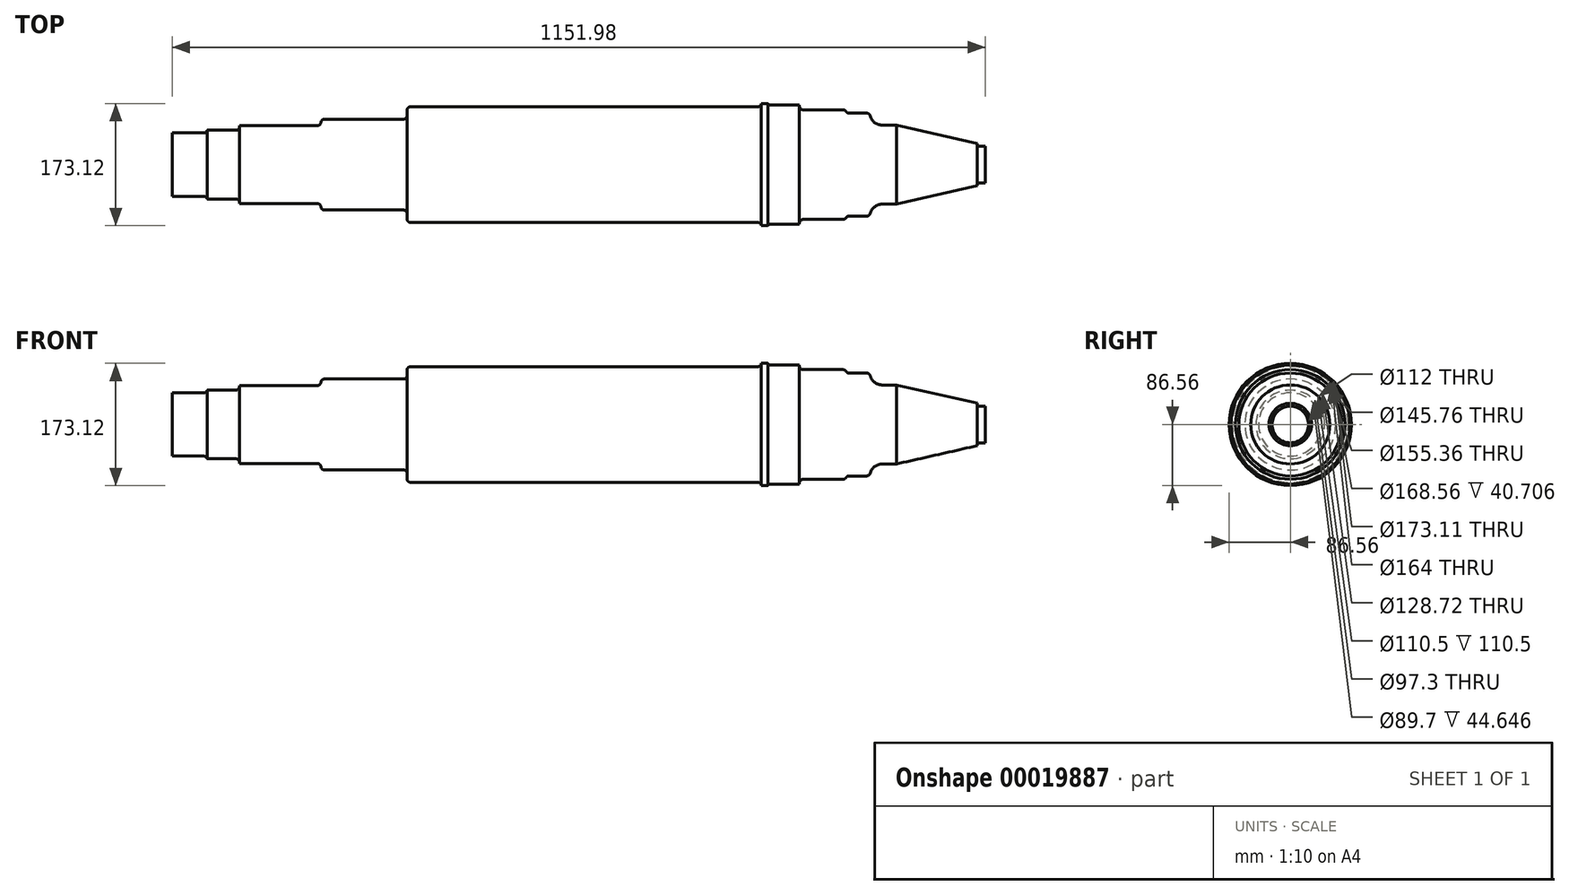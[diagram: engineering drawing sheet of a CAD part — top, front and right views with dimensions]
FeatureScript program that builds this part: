
annotation { "Feature Type Name" : "Feature", "Feature Type Description" : "" }
export const myFeature = defineFeature(function(context is Context, id is Id, definition is map)
    precondition{}
    {
        {
            var Q0;
            Q0=qCreatedBy(makeId("Front.planeOp"),FACE);
            var sketch = newSketch(context, id + "F0", { "sketchPlane" : qUnion([Q0])});
            skLineSegment(sketch, "E0", {"start": v(-457.72, 0) * mm, "end": v(-457.72, 44.85) * mm});
            skLineSegment(sketch, "E1", {"start": v(-457.72, 44.85) * mm, "end": v(-408.22, 44.85) * mm});
            skLineSegment(sketch, "E2", {"start": v(-408.22, 44.85) * mm, "end": v(-408.22, 48.65) * mm});
            skLineSegment(sketch, "E3", {"start": v(-408.22, 48.65) * mm, "end": v(-362.52, 48.65) * mm});
            skLineSegment(sketch, "E4", {"start": v(-362.52, 48.65) * mm, "end": v(-362.52, 55.25) * mm});
            skLineSegment(sketch, "E5", {"start": v(-362.52, 55.25) * mm, "end": v(-247.02, 55.25) * mm});
            skLineSegment(sketch, "E6", {"start": v(-247.02, 55.25) * mm, "end": v(-247.02, 64.36) * mm});
            skLineSegment(sketch, "E7", {"start": v(-247.02, 64.36) * mm, "end": v(-125.02, 64.36) * mm});
            skLineSegment(sketch, "E8", {"start": v(-125.02, 64.36) * mm, "end": v(-125.02, 82) * mm});
            skLineSegment(sketch, "E9", {"start": v(-125.02, 82) * mm, "end": v(376.98, 82) * mm});
            skLineSegment(sketch, "E10", {"start": v(376.98, 82) * mm, "end": v(376.98, 86.56) * mm});
            skLineSegment(sketch, "E11", {"start": v(376.98, 86.56) * mm, "end": v(386.1, 86.56) * mm});
            skLineSegment(sketch, "E12", {"start": v(386.1, 86.56) * mm, "end": v(386.1, 84.28) * mm});
            skLineSegment(sketch, "E13", {"start": v(386.1, 84.28) * mm, "end": v(431, 84.28) * mm});
            skLineSegment(sketch, "E14", {"start": v(431, 84.28) * mm, "end": v(431, 77.68) * mm});
            skLineSegment(sketch, "E15", {"start": v(431, 77.68) * mm, "end": v(496.26, 77.68) * mm});
            skLineSegment(sketch, "E16", {"start": v(496.26, 77.68) * mm, "end": v(496.26, 72.88) * mm});
            skLineSegment(sketch, "E17", {"start": v(496.26, 72.88) * mm, "end": v(531.26, 72.88) * mm});
            skLineSegment(sketch, "E18", {"start": v(531.26, 72.88) * mm, "end": v(531.26, 56) * mm});
            skLineSegment(sketch, "E19", {"start": v(-457.72, 0) * mm, "end": v(396.58, 0) * mm});
            skLineSegment(sketch, "E20", {"start": v(682.77, 25.86) * mm, "end": v(694.26, 26.1) * mm});
            skLineSegment(sketch, "E21", {"start": v(682.68, 30.06) * mm, "end": v(682.77, 25.86) * mm});
            skLineSegment(sketch, "E22", {"start": v(562, 0) * mm, "end": v(396.58, 0) * mm});
            skLineSegment(sketch, "E23", {"start": v(-502.65, 0) * mm, "end": v(562, 0) * mm, "construction": true});
            skPoint(sketch, "E23.startSnap0", {"position": v(-30.57, 0) * mm});
            skPoint(sketch, "E23.endSnap0", {"position": v(-30.57, 0) * mm});
            skLineSegment(sketch, "E24", {"start": v(732.2, 0) * mm, "end": v(-530.75, 0) * mm, "construction": true});
            skLineSegment(sketch, "E25", {"start": v(568.26, 56) * mm, "end": v(531.26, 56) * mm});
            skLineSegment(sketch, "E26", {"start": v(568.26, 56) * mm, "end": v(682.68, 30.06) * mm});
            skLineSegment(sketch, "E27", {"start": v(562, 0) * mm, "end": v(683.65, 0) * mm});
            skLineSegment(sketch, "E28", {"start": v(568.26, 56) * mm, "end": v(568.26, -19.91) * mm, "construction": true});
            skLineSegment(sketch, "E29", {"start": v(694.26, 26.1) * mm, "end": v(694.26, 0) * mm});
            skSolve(sketch);
        }
        {
            var Q0;
            Q0=sQuery(id+"F0.wireOp",EDGE,"E0");
            var Q1;
            Q1=sQuery(id+"F0.wireOp",EDGE,"E1");
            var Q2;
            Q2=sQuery(id+"F0.wireOp",EDGE,"E3");
            var Q3;
            Q3=sQuery(id+"F0.wireOp",EDGE,"E2");
            var Q4;
            Q4=sQuery(id+"F0.wireOp",EDGE,"E4");
            var Q5;
            Q5=sQuery(id+"F0.wireOp",EDGE,"E5");
            var Q6;
            Q6=sQuery(id+"F0.wireOp",EDGE,"E6");
            var Q7;
            Q7=sQuery(id+"F0.wireOp",EDGE,"E7");
            var Q8;
            Q8=sQuery(id+"F0.wireOp",EDGE,"E8");
            var Q9;
            Q9=sQuery(id+"F0.wireOp",EDGE,"E9");
            var Q10;
            Q10=sQuery(id+"F0.wireOp",EDGE,"E11");
            var Q11;
            Q11=sQuery(id+"F0.wireOp",EDGE,"E10");
            var Q12;
            Q12=sQuery(id+"F0.wireOp",EDGE,"E12");
            var Q13;
            Q13=sQuery(id+"F0.wireOp",EDGE,"E13");
            var Q14;
            Q14=sQuery(id+"F0.wireOp",EDGE,"E14");
            var Q15;
            Q15=sQuery(id+"F0.wireOp",EDGE,"E15");
            var Q16;
            Q16=sQuery(id+"F0.wireOp",EDGE,"E16");
            var Q17;
            Q17=sQuery(id+"F0.wireOp",EDGE,"E17");
            var Q18;
            Q18=sQuery(id+"F0.wireOp",EDGE,"E18");
            var Q19;
            Q19=sQuery(id+"F0.wireOp",EDGE,"1ff863c3-3cfa-4d4c-a43b-59d3ef948760");
            var Q20;
            Q20=sQuery(id+"F0.wireOp",EDGE,"E20");
            var Q21;
            Q21=sQuery(id+"F0.wireOp",EDGE,"E21");
            var Q22;
            Q22=sQuery(id+"F0.wireOp",EDGE,"605e6a14-245b-47b4-8274-c8cc4451a2e7");
            var Q23;
            Q23=sQuery(id+"F0.wireOp",EDGE,"E26");
            var Q24;
            Q24=sQuery(id+"F0.wireOp",EDGE,"E25");
            var Q25;
            Q25=sQuery(id+"F0.wireOp",EDGE,"E19");
            revolve(context, id + "F1", {"bodyType" : ToolBodyType.SURFACE, "surfaceEntities" : qUnion([Q0, Q1, Q2, Q3, Q4, Q5, Q6, Q7, Q8, Q9, Q10, Q11, Q12, Q13, Q14, Q15, Q16, Q17, Q18, Q19, Q20, Q21, Q22, Q23, Q24]), "axis" : qUnion([Q25]), "revolveType" : RevolveType.FULL});
        }
        {
            var Q0;
            Q0=makeQuery(id+"F1.opRevolve","SWEPT_EDGE",EDGE,{"disambiguationData":[OSD([sQuery(id+"F0.wireOp",VERTEX,"E2.start")])]});
            var Q1;
            Q1=makeQuery(id+"F1.opRevolve","SWEPT_EDGE",EDGE,{"disambiguationData":[OSD([sQuery(id+"F0.wireOp",VERTEX,"E4.start")])]});
            var Q2;
            Q2=makeQuery(id+"F1.opRevolve","SWEPT_EDGE",EDGE,{"disambiguationData":[OSD([sQuery(id+"F0.wireOp",VERTEX,"E6.start")])]});
            var Q3;
            Q3=makeQuery(id+"F1.opRevolve","SWEPT_EDGE",EDGE,{"disambiguationData":[OSD([sQuery(id+"F0.wireOp",VERTEX,"E8.start")])]});
            var Q4;
            Q4=makeQuery(id+"F1.opRevolve","SWEPT_EDGE",EDGE,{"disambiguationData":[OSD([sQuery(id+"F0.wireOp",VERTEX,"E10.start")])]});
            var Q5;
            Q5=makeQuery(id+"F1.opRevolve","SWEPT_FACE",FACE,{"disambiguationData":[OSD([sQuery(id+"F0.wireOp",EDGE,"E17")])]});
            var Q6;
            Q6=makeQuery(id+"F1.opRevolve","SWEPT_EDGE",EDGE,{"disambiguationData":[OSD([sQuery(id+"F0.wireOp",VERTEX,"E15.start")])]});
            var Q7;
            Q7=makeQuery(id+"F1.opRevolve","SWEPT_EDGE",EDGE,{"disambiguationData":[OSD([sQuery(id+"F0.wireOp",VERTEX,"E13.start")])]});
            fillet(context, id + "F2", {"entities" : qUnion([Q0, Q1, Q2, Q3, Q4, Q5, Q6, Q7]), "radius" : 5 * mm, "tangentPropagation" : true, "allowEdgeOverflow" : false});
        }
        {
            var Q0;
            Q0=makeQuery(id+"F1.opRevolve","SWEPT_EDGE",EDGE,{"disambiguationData":[OSD([sQuery(id+"F0.wireOp",VERTEX,"E9.start")])]});
            var Q1;
            Q1=makeQuery(id+"F1.opRevolve","SWEPT_EDGE",EDGE,{"disambiguationData":[OSD([sQuery(id+"F0.wireOp",VERTEX,"E7.start")])]});
            var Q2;
            Q2=makeQuery(id+"F2.opFillet","BLEND_EDGE",EDGE,{"blendedFrom":[makeQuery(id+"F1.opRevolve","SWEPT_EDGE",EDGE,{"disambiguationData":[OSD([sQuery(id+"F0.wireOp",VERTEX,"E15.start")])]}),makeQuery(id+"F1.opRevolve","SWEPT_FACE",FACE,{"disambiguationData":[OSD([sQuery(id+"F0.wireOp",EDGE,"E14")])]})],"blendedInto":[makeQuery(id+"F1.opRevolve","SWEPT_FACE",FACE,{"disambiguationData":[OSD([sQuery(id+"F0.wireOp",EDGE,"E14")])]})]});
            var Q3;
            Q3=makeQuery(id+"F2.opFillet","BLEND_EDGE",EDGE,{"blendedFrom":[makeQuery(id+"F1.opRevolve","SWEPT_EDGE",EDGE,{"disambiguationData":[OSD([sQuery(id+"F0.wireOp",VERTEX,"E17.start")])]}),makeQuery(id+"F1.opRevolve","SWEPT_FACE",FACE,{"disambiguationData":[OSD([sQuery(id+"F0.wireOp",EDGE,"E15")])]})],"blendedInto":[makeQuery(id+"F1.opRevolve","SWEPT_FACE",FACE,{"disambiguationData":[OSD([sQuery(id+"F0.wireOp",EDGE,"E15")])]})]});
            fillet(context, id + "F3", {"entities" : qUnion([Q0, Q1, Q2, Q3]), "radius" : 5 * mm, "tangentPropagation" : true, "allowEdgeOverflow" : false});
        }
        {
            var Q0;
            Q0=makeQuery(id+"F1.opRevolve","SWEPT_EDGE",EDGE,{"disambiguationData":[OSD([sQuery(id+"F0.wireOp",VERTEX,"E25.end")])]});
            fillet(context, id + "F4", {"entities" : qUnion([Q0]), "radius" : 17.8 * mm, "tangentPropagation" : true, "allowEdgeOverflow" : false});
        }
    });
